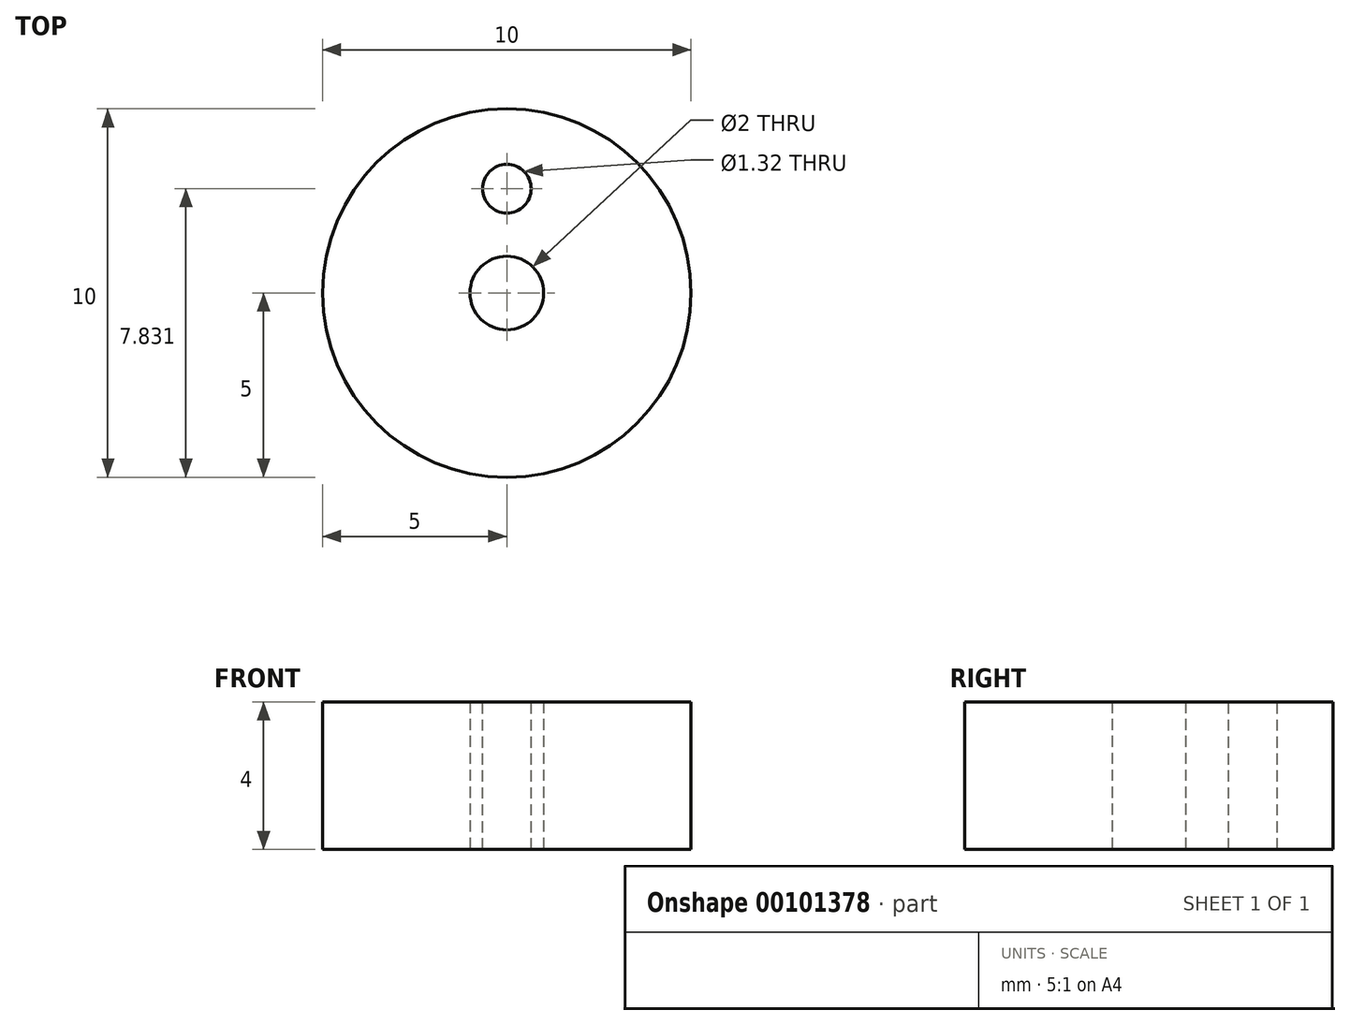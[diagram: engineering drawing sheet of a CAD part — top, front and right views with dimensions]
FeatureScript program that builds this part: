
annotation { "Feature Type Name" : "Feature", "Feature Type Description" : "" }
export const myFeature = defineFeature(function(context is Context, id is Id, definition is map)
    precondition{}
    {
        {
            var Q0;
            Q0=qCreatedBy(makeId("Top.planeOp"),FACE);
            var sketch = newSketch(context, id + "F0", { "sketchPlane" : qUnion([Q0])});
            skCircle(sketch, "E0", {"center": v(0, 0) * mm, "radius": 1 * mm});
            skCircle(sketch, "E1", {"center": v(0, 0) * mm, "radius": 5 * mm});
            skSolve(sketch);
        }
        {
            var Q0;
            Q0=makeQuery(id+"F0.imprint","IMPRINT",FACE,{"disambiguationData":[TD([[makeQuery(id+"F0.imprint","IMPRINT",EDGE,{"derivedFrom":sQuery(id+"F0.wireOp",EDGE,"E0")}),-1.0]])]});
            extrude(context, id + "F1", {"entities" : qUnion([Q0]), "depth" : 4 * mm});
        }
        {
            var Q0;
            Q0=makeQuery(id+"F1.opExtrude","CAP_FACE",FACE,{"disambiguationData":[OSD([sQuery(id+"F0.wireOp",EDGE,"E0"),sQuery(id+"F0.wireOp",EDGE,"E1")])],"isStart":false});
            var sketch = newSketch(context, id + "F2", { "sketchPlane" : qUnion([Q0])});
            skCircle(sketch, "E2", {"center": v(0, 2.83) * mm, "radius": 0.66 * mm});
            skSolve(sketch);
        }
        {
            var Q0;
            Q0=makeQuery(id+"F2.imprint","IMPRINT",FACE,{"disambiguationData":[TD([[makeQuery(id+"F2.imprint","IMPRINT",EDGE,{"derivedFrom":sQuery(id+"F2.wireOp",EDGE,"E2")}),1.0]])]});
            var Q1;
            Q1=makeQuery(id+"F1.opExtrude","CAP_FACE",FACE,{"disambiguationData":[OSD([sQuery(id+"F0.wireOp",EDGE,"E0"),sQuery(id+"F0.wireOp",EDGE,"E1")])],"isStart":true});
            extrude(context, id + "F3", {"entities" : qUnion([Q0]), "operationType" : NewBodyOperationType.REMOVE, "oppositeDirection" : true, "endBoundEntityFace" : qUnion([Q1]), "depth" : 10.72 * mm});
        }
    });
